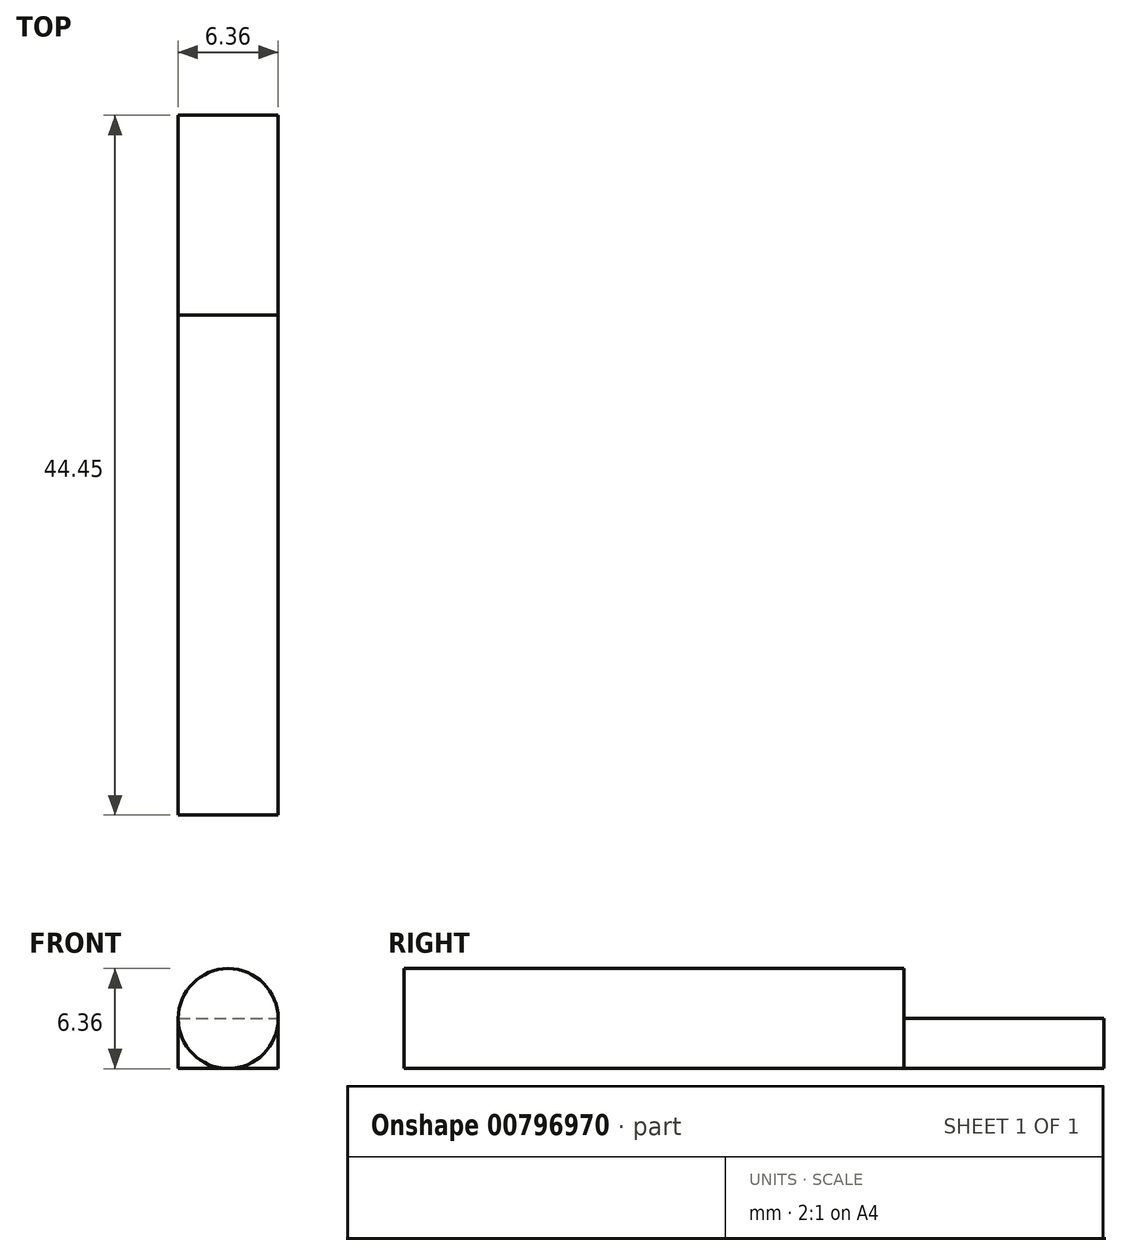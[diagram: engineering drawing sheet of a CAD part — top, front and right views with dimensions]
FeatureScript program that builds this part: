
annotation { "Feature Type Name" : "Feature", "Feature Type Description" : "" }
export const myFeature = defineFeature(function(context is Context, id is Id, definition is map)
    precondition{}
    {
        {
            var Q0;
            Q0=qCreatedBy(makeId("Front.planeOp"),FACE);
            var sketch = newSketch(context, id + "F0", { "sketchPlane" : qUnion([Q0])});
            skCircle(sketch, "E0", {"center": v(0, 0) * mm, "radius": 3.18 * mm});
            skSolve(sketch);
        }
        {
            var Q0;
            Q0=makeQuery(id+"F0.imprint","IMPRINT",FACE,{"disambiguationData":[TD([[makeQuery(id+"F0.imprint","IMPRINT",EDGE,{"derivedFrom":sQuery(id+"F0.wireOp",EDGE,"E0")}),1.0]])]});
            extrude(context, id + "F1", {"entities" : qUnion([Q0]), "depth" : 31.75 * mm, "offsetDistance" : 25.4 * mm});
        }
        {
            var Q0;
            Q0=qCreatedBy(makeId("Top.planeOp"),FACE);
            var sketch = newSketch(context, id + "F2", { "sketchPlane" : qUnion([Q0])});
            skLineSegment(sketch, "E1.bottom", {"start": v(-3.18, 12.7) * mm, "end": v(3.18, 12.7) * mm});
            skLineSegment(sketch, "E1.top", {"start": v(-3.18, 0) * mm, "end": v(3.18, 0) * mm});
            skLineSegment(sketch, "E1.left", {"start": v(-3.18, 12.7) * mm, "end": v(-3.18, 0) * mm});
            skLineSegment(sketch, "E1.right", {"start": v(3.17, 12.7) * mm, "end": v(3.17, 0) * mm});
            skSolve(sketch);
        }
        {
            var Q0;
            Q0=makeQuery(id+"F2.imprint","IMPRINT",FACE,{"disambiguationData":[TD([[makeQuery(id+"F2.imprint","IMPRINT",EDGE,{"derivedFrom":sQuery(id+"F2.wireOp",EDGE,"E1.bottom")}),-1.0]])]});
            extrude(context, id + "F3", {"entities" : qUnion([Q0]), "operationType" : NewBodyOperationType.ADD, "oppositeDirection" : true, "depth" : 3.17 * mm, "offsetDistance" : 25.4 * mm});
        }
    });
